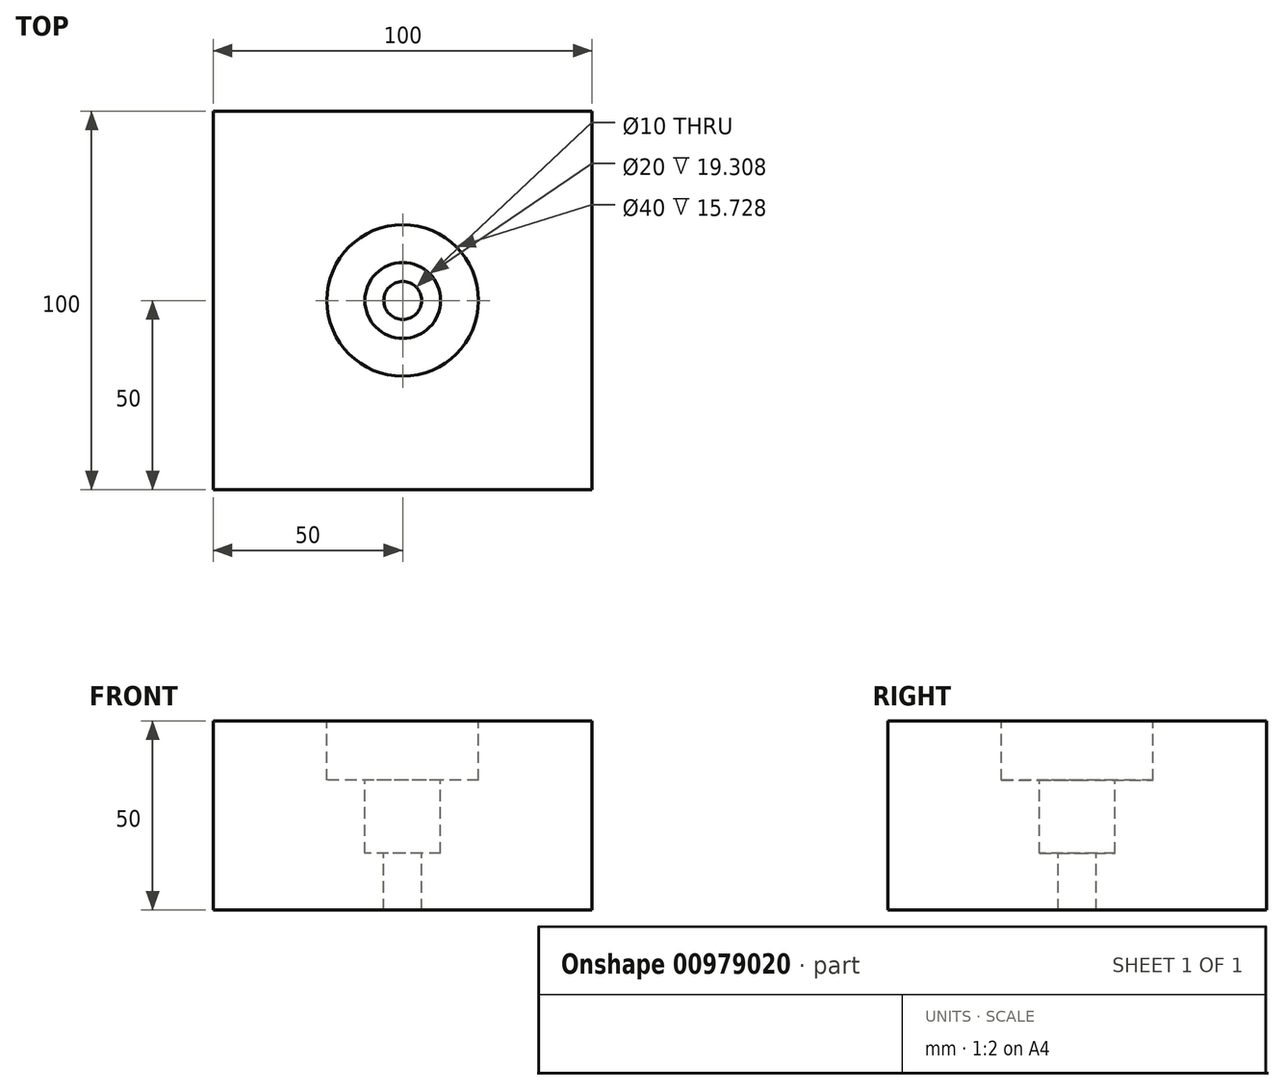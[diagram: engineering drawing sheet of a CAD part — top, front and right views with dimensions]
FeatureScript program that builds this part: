
annotation { "Feature Type Name" : "Feature", "Feature Type Description" : "" }
export const myFeature = defineFeature(function(context is Context, id is Id, definition is map)
    precondition{}
    {
        {
            var Q0;
            Q0=qCreatedBy(makeId("Top.planeOp"),FACE);
            var sketch = newSketch(context, id + "F0", { "sketchPlane" : qUnion([Q0])});
            skLineSegment(sketch, "E0.bottom", {"start": v(50, 50) * mm, "end": v(-50, 50) * mm});
            skLineSegment(sketch, "E0.top", {"start": v(50, -50) * mm, "end": v(-50, -50) * mm});
            skLineSegment(sketch, "E0.left", {"start": v(50, 50) * mm, "end": v(50, -50) * mm});
            skLineSegment(sketch, "E0.right", {"start": v(-50, 50) * mm, "end": v(-50, -50) * mm});
            skPoint(sketch, "E0.middle", {"position": v(0, 0) * mm});
            skSolve(sketch);
        }
        {
            var Q0;
            Q0=makeQuery(id+"F0.imprint","IMPRINT",FACE,{"disambiguationData":[TD([[makeQuery(id+"F0.imprint","IMPRINT",EDGE,{"derivedFrom":sQuery(id+"F0.wireOp",EDGE,"E0.bottom")}),1.0]])]});
            extrude(context, id + "F1", {"entities" : qUnion([Q0]), "oppositeDirection" : true, "depth" : 50 * mm, "offsetDistance" : 25 * mm});
        }
        {
            var Q0;
            Q0=qCreatedBy(makeId("Right.planeOp"),FACE);
            var sketch = newSketch(context, id + "F2", { "sketchPlane" : qUnion([Q0])});
            skLineSegment(sketch, "E1", {"start": v(0, 25.27) * mm, "end": v(0, 0) * mm, "construction": true});
            skLineSegment(sketch, "E2", {"start": v(0, 0) * mm, "end": v(20, 0) * mm});
            skLineSegment(sketch, "E3", {"start": v(20, 0) * mm, "end": v(20, -15.73) * mm});
            skLineSegment(sketch, "E4", {"start": v(20, -15.73) * mm, "end": v(10, -15.73) * mm});
            skLineSegment(sketch, "E5", {"start": v(10, -15.73) * mm, "end": v(10, -35.04) * mm});
            skLineSegment(sketch, "E6", {"start": v(10, -35.04) * mm, "end": v(5, -35.04) * mm});
            skLineSegment(sketch, "E7", {"start": v(5, -35.04) * mm, "end": v(5, -50) * mm});
            skLineSegment(sketch, "E8", {"start": v(5, -50) * mm, "end": v(0, -50) * mm});
            skLineSegment(sketch, "E9.trimOffspring", {"start": v(0, -50) * mm, "end": v(0, -62.15) * mm, "construction": true});
            skLineSegment(sketch, "E10", {"start": v(0, 0) * mm, "end": v(0, -50) * mm});
            skSolve(sketch);
        }
        {
            var Q0;
            Q0=makeQuery(id+"F2.imprint","IMPRINT",FACE,{"disambiguationData":[TD([[makeQuery(id+"F2.imprint","IMPRINT",EDGE,{"derivedFrom":sQuery(id+"F2.wireOp",EDGE,"E2")}),-1.0]])]});
            var Q1;
            Q1=sQuery(id+"F2.wireOp",EDGE,"E1");
            revolve(context, id + "F3", {"operationType" : NewBodyOperationType.REMOVE, "surfaceOperationType" : NewSurfaceOperationType.NEW, "entities" : qUnion([Q0]), "axis" : qUnion([Q1]), "revolveType" : RevolveType.FULL});
        }
    });
